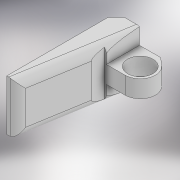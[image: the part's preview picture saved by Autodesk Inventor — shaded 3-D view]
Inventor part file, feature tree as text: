
AUTODESK INVENTOR PART (.ipt)
format: ipt  version: 2022 (Build 260153000, 153)  size: 149,504 bytes
history: native  units: mm
features: extrude x2, sketch x1, fillet x1, chamfer x1
ambient origin geometry x8: Origin, YZ Plane, XZ Plane, XY Plane, X Axis, Y Axis, Z Axis, Center Point
bodies: Solid1 (feature_tree)
feature tree (5):
  sketch  "Sketch1"  dims[d0=5.5mm d1=5.0mm d2=2.5mm d3=10.5mm d4=7.2mm d5=6.0mm d6=4.1mm d7=0.0mm d8=12.0mm d9=0.0mm d10=2.0mm d11=2.0mm d12=2.0mm d13=45.0deg d14=4.23mm]
  extrude  "Extrusion1"  Depth=5.0mm
  extrude  "Extrusion2"  Depth=2.0mm
  fillet  "Fillet1"  Radius=10.5mm
  chamfer  "Chamfer1"  Distance=7.2mm
